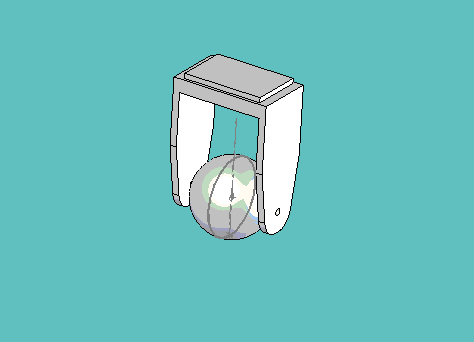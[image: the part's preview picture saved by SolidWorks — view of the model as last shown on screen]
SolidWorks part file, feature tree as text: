
SOLIDWORKS PART (.sldprt)
format: sldprt  version: not decoded by parser v0  size: 553,984 bytes
history: native  units: mm
features: sketch x6, extrude x4, material x1, revolve x1 (+11 scaffold rows collapsed)
feature tree (23):
  scaffold x11  (default folders/planes/origin — collapsed)
  material  "Material <not specified>"
  sketch  "Sketch1"  dims[D1=38.1mm D2=25.4mm]
  extrude  "Extrude1"  Depth=2.38125mm
  sketch  "Sketch2"  dims[D1=1.5875mm D2=1.5875mm D3=4.2672mm D4=4.2672mm]
  extrude  "Extrude2"  Depth=6.35mm
  sketch  "Sketch3"  dims[D2=3.175mm D7=22.225mm D1=47.625mm D3=9.525mm D4=6.35mm D5=25.4mm D6=23.8125mm]
  extrude  "Extrude3"  Depth=3.175mm
  sketch  "Sketch4"  dims[D1=0.0mm]
  extrude  "Extrude4"  Depth=3.175mm
  sketch  "Sketch5"  dims[D1=36.068mm]
  revolve  "Revolve1"  Angle=360deg
  sketch  "Sketch6"
decode coverage: 10 of 11 modeling features carry decoded parameters
note: suppression state not decoded; provenance and decode notes live in map.json
